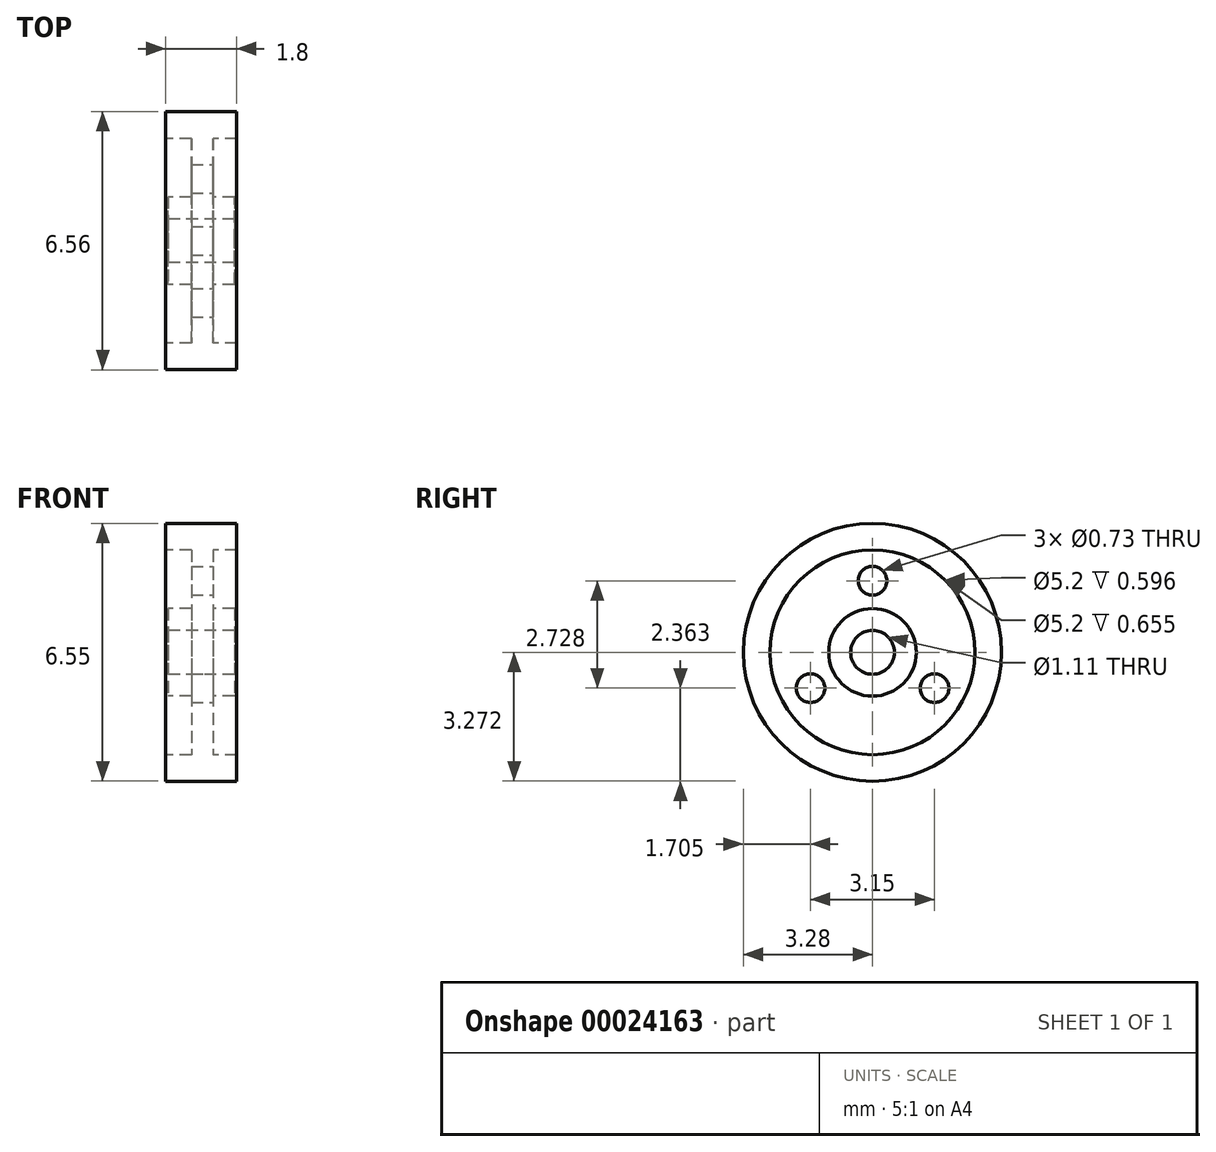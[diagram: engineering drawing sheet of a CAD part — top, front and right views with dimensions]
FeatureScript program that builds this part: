
annotation { "Feature Type Name" : "Feature", "Feature Type Description" : "" }
export const myFeature = defineFeature(function(context is Context, id is Id, definition is map)
    precondition{}
    {
        {
            var Q0;
            Q0=qCreatedBy(makeId("Front.planeOp"),FACE);
            var sketch = newSketch(context, id + "F0", { "sketchPlane" : qUnion([Q0])});
            skLineSegment(sketch, "E0", {"start": v(-3.36, -0.33) * mm, "end": v(2.12, -0.33) * mm, "construction": true});
            skLineSegment(sketch, "E1.bottom", {"start": v(-2.24, 0.23) * mm, "end": v(-0.56, 0.23) * mm});
            skLineSegment(sketch, "E1.top", {"start": v(-2.24, 0.78) * mm, "end": v(-0.56, 0.78) * mm});
            skLineSegment(sketch, "E1.left", {"start": v(-2.24, 0.23) * mm, "end": v(-2.24, 0.78) * mm});
            skLineSegment(sketch, "E1.right", {"start": v(-0.56, 0.23) * mm, "end": v(-0.56, 0.78) * mm});
            skLineSegment(sketch, "E2.bottom", {"start": v(-1.65, 0.78) * mm, "end": v(-1.1, 0.78) * mm});
            skLineSegment(sketch, "E2.top", {"start": v(-1.65, 2.27) * mm, "end": v(-1.1, 2.27) * mm});
            skLineSegment(sketch, "E2.left", {"start": v(-1.65, 0.78) * mm, "end": v(-1.65, 2.27) * mm});
            skLineSegment(sketch, "E2.right", {"start": v(-1.1, 0.78) * mm, "end": v(-1.1, 2.27) * mm});
            skLineSegment(sketch, "E3.bottom", {"start": v(-2.3, 2.27) * mm, "end": v(-0.5, 2.27) * mm});
            skLineSegment(sketch, "E3.top", {"start": v(-2.3, 2.95) * mm, "end": v(-0.5, 2.95) * mm});
            skLineSegment(sketch, "E3.left", {"start": v(-2.3, 2.27) * mm, "end": v(-2.3, 2.95) * mm});
            skLineSegment(sketch, "E3.right", {"start": v(-0.5, 2.27) * mm, "end": v(-0.5, 2.95) * mm});
            skSolve(sketch);
        }
        {
            var Q0;
            Q0 = qSketchRegion(id + "F0", true);
            var Q1;
            Q1=sQuery(id+"F0.wireOp",EDGE,"E0");
            revolve(context, id + "F1", {"entities" : qUnion([Q0]), "axis" : qUnion([Q1]), "revolveType" : RevolveType.FULL});
        }
        {
            var Q0;
            Q0=makeQuery(id+"F1.opRevolve","SWEPT_FACE",FACE,{"disambiguationData":[OSD([sQuery(id+"F0.wireOp",EDGE,"E1.right")])]});
            var sketch = newSketch(context, id + "F2", { "sketchPlane" : qUnion([Q0])});
            skCircle(sketch, "E4", {"center": v(0, 1.5) * mm, "radius": 0.36 * mm});
            skCircle(sketch, "E5.1.0", {"center": v(-1.58, -1.24) * mm, "radius": 0.36 * mm});
            skCircle(sketch, "E5.2.0", {"center": v(1.58, -1.24) * mm, "radius": 0.36 * mm});
            skPoint(sketch, "E5.center", {"position": v(0, -0.33) * mm});
            skSolve(sketch);
        }
        {
            var Q0;
            Q0=makeQuery(id+"F2.imprint","IMPRINT",FACE,{"disambiguationData":[TD([[makeQuery(id+"F2.imprint","IMPRINT",EDGE,{"derivedFrom":sQuery(id+"F2.wireOp",EDGE,"E4")}),1.0]])]});
            var Q1;
            Q1=makeQuery(id+"F2.imprint","IMPRINT",FACE,{"disambiguationData":[TD([[makeQuery(id+"F2.imprint","IMPRINT",EDGE,{"derivedFrom":sQuery(id+"F2.wireOp",EDGE,"E5.2.0")}),1.0]])]});
            var Q2;
            Q2=makeQuery(id+"F2.imprint","IMPRINT",FACE,{"disambiguationData":[TD([[makeQuery(id+"F2.imprint","IMPRINT",EDGE,{"derivedFrom":sQuery(id+"F2.wireOp",EDGE,"E5.1.0")}),1.0]])]});
            extrude(context, id + "F3", {"entities" : qUnion([Q0, Q1, Q2]), "operationType" : NewBodyOperationType.REMOVE, "endBound" : BoundingType.THROUGH_ALL, "oppositeDirection" : true, "depth" : 25.4 * mm});
        }
    });
